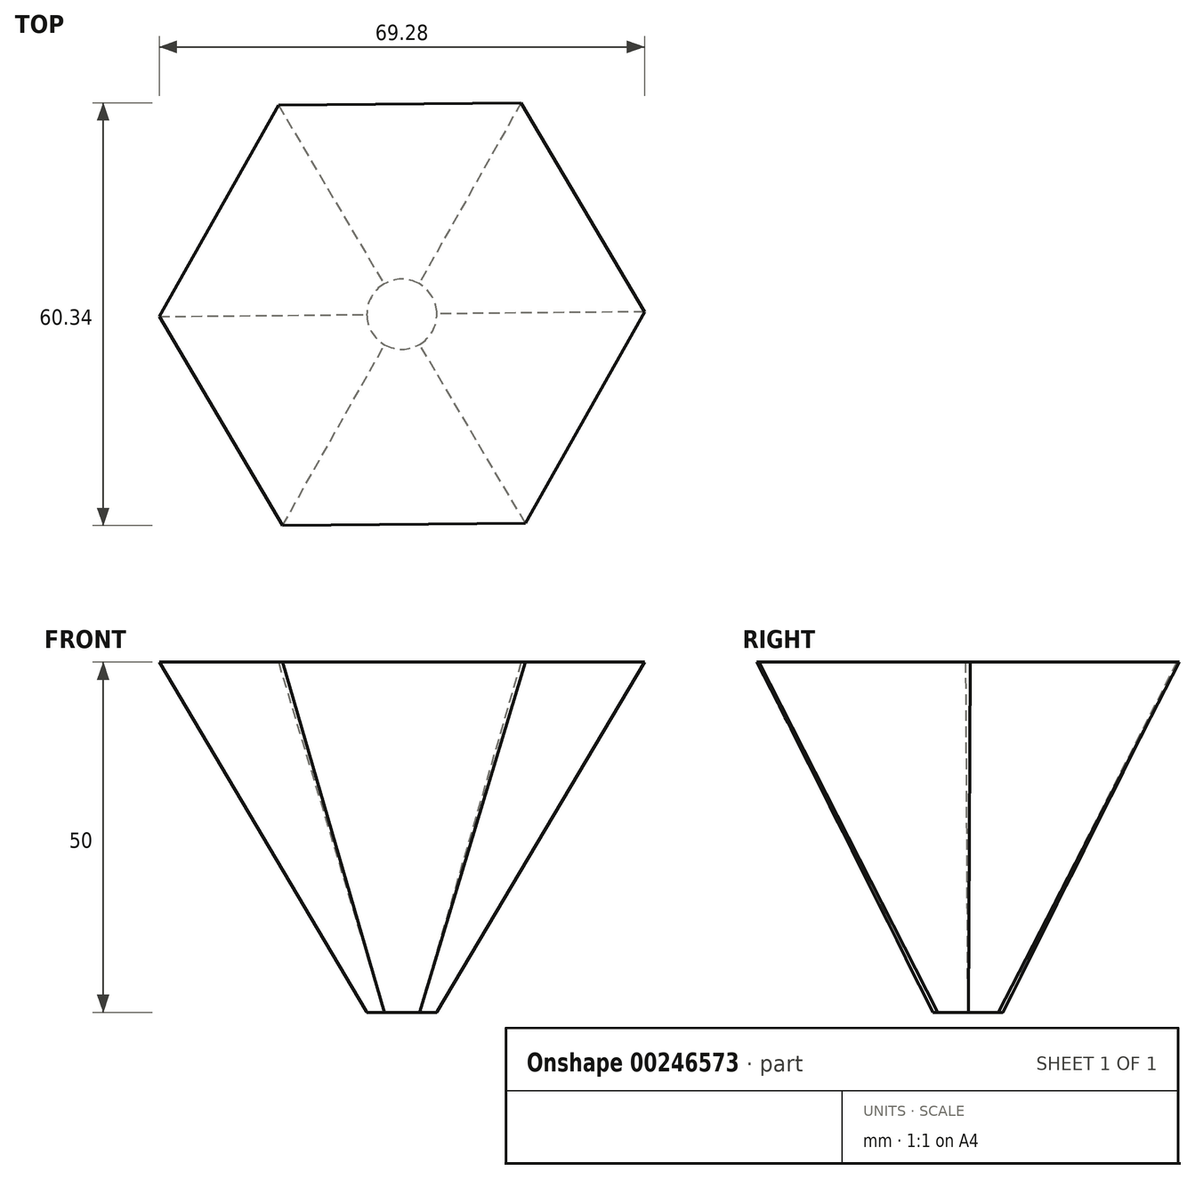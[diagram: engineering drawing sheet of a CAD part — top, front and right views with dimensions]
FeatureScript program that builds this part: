
annotation { "Feature Type Name" : "Feature", "Feature Type Description" : "" }
export const myFeature = defineFeature(function(context is Context, id is Id, definition is map)
    precondition{}
    {
        {
            var Q0;
            Q0=qCreatedBy(makeId("Top.planeOp"),FACE);
            var sketch = newSketch(context, id + "F0", { "sketchPlane" : qUnion([Q0])});
            skCircle(sketch, "E0", {"center": v(0, 0) * mm, "radius": 5 * mm});
            skSolve(sketch);
        }
        {
            var Q0;
            Q0=qCreatedBy(makeId("Top.planeOp"),FACE);
            cPlane(context, id + "F1", {"entities" : qUnion([Q0]), "cplaneType" : CPlaneType.OFFSET, "offset" : 25 * mm, "width" : 150 * mm, "height" : 150 * mm});
        }
        {
            var Q0;
            Q0=qCreatedBy(id+"F1.planeOp",FACE);
            cPlane(context, id + "F2", {"entities" : qUnion([Q0]), "cplaneType" : CPlaneType.OFFSET, "offset" : 25 * mm, "width" : 150 * mm, "height" : 150 * mm});
        }
        {
            var Q0;
            Q0=qCreatedBy(id+"F2.planeOp",FACE);
            var sketch = newSketch(context, id + "F3", { "sketchPlane" : qUnion([Q0])});
            skCircle(sketch, "E1.cCircle", {"center": v(0, 0) * mm, "radius": 30 * mm, "construction": true});
            skLineSegment(sketch, "E1.0", {"start": v(34.64, 0.34) * mm, "end": v(17.62, -29.83) * mm});
            skLineSegment(sketch, "E1.1", {"start": v(17.62, -29.83) * mm, "end": v(-17.02, -30.17) * mm});
            skLineSegment(sketch, "E1.2", {"start": v(-17.02, -30.17) * mm, "end": v(-34.64, -0.34) * mm});
            skLineSegment(sketch, "E1.3", {"start": v(-34.64, -0.34) * mm, "end": v(-17.62, 29.83) * mm});
            skLineSegment(sketch, "E1.4", {"start": v(-17.62, 29.83) * mm, "end": v(17.02, 30.17) * mm});
            skLineSegment(sketch, "E1.5", {"start": v(17.02, 30.17) * mm, "end": v(34.64, 0.34) * mm});
            skPoint(sketch, "E1.0.midPoint", {"position": v(26.13, -14.74) * mm});
            skSolve(sketch);
        }
        {
            var Q0;
            Q0=makeQuery(id+"F3.imprint","IMPRINT",FACE,{"disambiguationData":[TD([[makeQuery(id+"F3.imprint","IMPRINT",EDGE,{"derivedFrom":sQuery(id+"F3.wireOp",EDGE,"E1.0")}),-1.0]])]});
            var Q1;
            Q1=makeQuery(id+"F0.imprint","IMPRINT",FACE,{"disambiguationData":[TD([[makeQuery(id+"F0.imprint","IMPRINT",EDGE,{"derivedFrom":sQuery(id+"F0.wireOp",EDGE,"E0")}),1.0]])]});
            loft(context, id + "F4", {"sheetProfilesArray" : [{ "sheetProfileEntities" : qUnion([Q0]) }, { "sheetProfileEntities" : qUnion([Q1]) }]});
        }
    });
